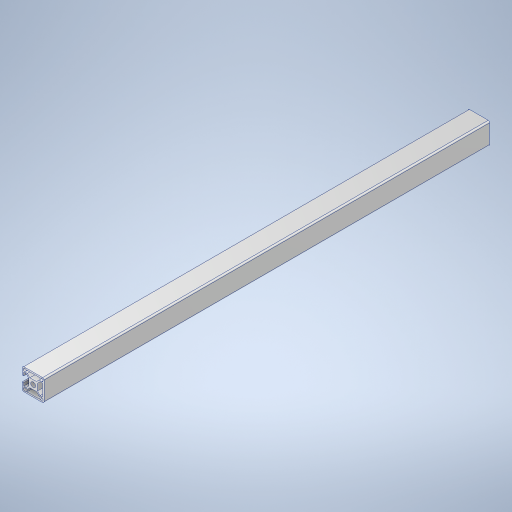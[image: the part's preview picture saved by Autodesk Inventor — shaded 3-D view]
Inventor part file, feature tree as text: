
AUTODESK INVENTOR PART (.ipt)
format: ipt  version: 2024 (Build 280153000, 153)  size: 372,736 bytes
history: native  units: mm
features: other x21, sketch x4, extrude x3, thread x2, hole x1
ambient origin geometry x8: Origin, YZ Plane, XZ Plane, XY Plane, X Axis, Y Axis, Z Axis, Center Point
bodies: Solid1 (feature_tree)
feature tree (31):
  extrude  "Extrusion1"  Depth=600.0mm TaperAngle=0.0deg
  hole  "Hole1"  [1 undecoded]
  extrude  "Extrusion2"  TaperAngle=0.0deg  [1 undecoded]
  extrude  "Extrusion3"  Depth=10.0mm TaperAngle=0.0deg
  other  "C1_XY"
  other  "C1_YZ"
  other  "C1_ZX"
  other  "C1_X"
  other  "C1_Y"
  other  "C1_Z"
  other  "C1_Center"
  other  "to_frame_cap1_XY"
  other  "to_frame_cap1_YZ"
  other  "to_frame_cap1_ZX"
  other  "to_frame_cap1_X"
  other  "to_frame_cap1_Y"
  other  "to_frame_cap1_Z"
  other  "to_frame_cap1_Center"
  other  "to_frame_cap2_XY"
  other  "to_frame_cap2_YZ"
  other  "to_frame_cap2_ZX"
  other  "to_frame_cap2_X"
  other  "to_frame_cap2_Y"
  other  "to_frame_cap2_Z"
  other  "to_frame_cap2_Center"
  thread  "Thread1"  [1 undecoded]
  thread  "Thread2"  [1 undecoded]
  sketch  "Sketch_122"  dims[d2=6.8mm d3=6.0mm d4=4.0mm d5=2.0mm d6=90.0deg d7=600.0mm d8=0.0mm d9=600.0mm d10=0.0mm]
  sketch  "Sketch2"  dims[d0=616.0mm d1=0.0mm]
  sketch  "Sketch_173"  dims[d11=600.0mm d12=0.0mm d13=0.0mm]
  sketch  "Sketch_174"  dims[d14=0.0mm d15=0.0mm d16=10.0mm d17=0.0mm d18=10.0mm d19=0.0mm]
note: 4 required parameter values undecoded (feature->parameter linkage not recoverable at this tier; creation-order binding heuristic only, values carry confidence <= 0.55)
